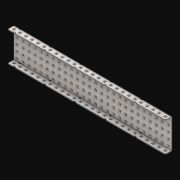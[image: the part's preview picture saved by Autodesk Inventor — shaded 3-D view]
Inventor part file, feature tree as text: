
AUTODESK INVENTOR PART (.ipt)
format: ipt  version: 2021 (Build 250183000, 183)  size: 3,637,248 bytes
history: native  units: in
note: dims shown in document units (in); Inventor stores cm internally (conversion verified against a paired STEP export)
features: extrude x183, other x182, sketch x4, thicken_offset x3, pattern_linear x3, imported_body x1
ambient origin geometry x8: Origin, YZ Plane, XZ Plane, XY Plane, X Axis, Y Axis, Z Axis, Center Point
bodies: Solid1 (feature_tree)
feature tree (376):
  thicken_offset  "Thicken1"
  thicken_offset  "Thicken2"
  thicken_offset  "Thicken3"
  pattern_linear  "Rectangular Pattern1"  Spacing1=0.001in  [1 undecoded]
  pattern_linear  "Rectangular Pattern2"  Spacing1=0.001in  [1 undecoded]
  pattern_linear  "Rectangular Pattern3"  Spacing1=0.182in  [1 undecoded]
  extrude  "Extrusion1"  Depth=0.063in TaperAngle=0.0deg
  sketch  "Sketch1"  dims[d0=0.001in]
  other  "Srf1"
  sketch  "Sketch2"  dims[d1=0.001in]
  other  "Srf2"
  sketch  "Sketch3"  dims[d2=0.001in]
  other  "Srf3"
  other  "Srf4"
  other  "Srf5"
  other  "Srf6"
  other  "Srf7"
  other  "Srf8"
  other  "Srf9"
  other  "Srf10"
  other  "Srf11"
  other  "Srf12"
  other  "Srf13"
  other  "Srf14"
  other  "Srf15"
  other  "Srf16"
  other  "Srf17"
  other  "Srf18"
  other  "Srf19"
  other  "Srf20"
  other  "Srf21"
  other  "Srf22"
  other  "Srf23"
  other  "Srf24"
  other  "Srf25"
  other  "Srf26"
  other  "Srf27"
  other  "Srf28"
  other  "Srf38"
  other  "Srf39"
  other  "Srf40"
  other  "Srf41"
  other  "Srf42"
  other  "Srf43"
  other  "Srf44"
  other  "Srf45"
  other  "Srf46"
  other  "Srf47"
  other  "Srf48"
  other  "Srf49"
  other  "Srf50"
  other  "Srf51"
  other  "Srf52"
  other  "Srf53"
  other  "Srf54"
  other  "Srf55"
  other  "Srf56"
  other  "Srf57"
  other  "Srf58"
  other  "Srf59"
  other  "Srf60"
  other  "Srf61"
  other  "Srf62"
  other  "Srf72"
  other  "Srf73"
  other  "Srf74"
  other  "Srf75"
  other  "Srf76"
  other  "Srf77"
  other  "Srf78"
  other  "Srf79"
  other  "Srf80"
  other  "Srf81"
  other  "Srf82"
  other  "Srf83"
  other  "Srf84"
  other  "Srf85"
  other  "Srf86"
  other  "Srf87"
  other  "Srf88"
  other  "Srf89"
  other  "Srf90"
  other  "Srf91"
  other  "Srf92"
  other  "Srf93"
  other  "Srf94"
  other  "Srf95"
  other  "Srf96"
  other  "Srf106"
  other  "Srf107"
  other  "Srf108"
  other  "Srf109"
  other  "Srf110"
  other  "Srf111"
  other  "Srf112"
  other  "Srf113"
  other  "Srf114"
  other  "Srf115"
  other  "Srf116"
  other  "Srf117"
  other  "Srf118"
  other  "Srf119"
  other  "Srf120"
  other  "Srf121"
  other  "Srf122"
  other  "Srf123"
  other  "Srf124"
  other  "Srf125"
  other  "Srf126"
  other  "Srf127"
  other  "Srf128"
  other  "Srf129"
  other  "Srf130"
  other  "Srf131"
  other  "Srf141"
  other  "Srf142"
  other  "Srf143"
  other  "Srf144"
  other  "Srf145"
  other  "Srf146"
  other  "Srf147"
  other  "Srf148"
  other  "Srf149"
  other  "Srf150"
  other  "Srf151"
  other  "Srf152"
  other  "Srf153"
  other  "Srf154"
  other  "Srf155"
  other  "Srf156"
  other  "Srf157"
  other  "Srf158"
  other  "Srf159"
  other  "Srf160"
  other  "Srf161"
  other  "Srf162"
  other  "Srf163"
  other  "Srf164"
  other  "Srf165"
  other  "Srf166"
  other  "Srf176"
  other  "Srf177"
  other  "Srf178"
  other  "Srf179"
  other  "Srf180"
  other  "Srf181"
  other  "Srf182"
  other  "Srf183"
  other  "Srf184"
  other  "Srf185"
  other  "Srf186"
  other  "Srf187"
  other  "Srf188"
  other  "Srf189"
  other  "Srf190"
  other  "Srf191"
  other  "Srf192"
  other  "Srf193"
  other  "Srf194"
  other  "Srf195"
  other  "Srf196"
  other  "Srf197"
  other  "Srf198"
  other  "Srf199"
  other  "Srf200"
  other  "Srf201"
  other  "Srf211"
  other  "Srf212"
  other  "Srf213"
  other  "Srf214"
  other  "Srf215"
  other  "Srf216"
  other  "Srf217"
  other  "Srf218"
  other  "Srf219"
  other  "Srf220"
  other  "Srf221"
  other  "Srf222"
  other  "Srf223"
  other  "Srf224"
  other  "Srf225"
  other  "Srf226"
  other  "Srf227"
  other  "Srf228"
  other  "Srf229"
  other  "Srf230"
  other  "Srf231"
  other  "Srf232"
  other  "Srf233"
  other  "Srf234"
  other  "Srf235"
  other  "Srf236"
  sketch  "Sketch4"  dims[d3=0.001in d4=0.001in d5=0.001in d6=0.182in d7=0.063in d8=0.0in d9=0.182in d10=0.063in d11=0.0in d12=0.182in d13=0.063in d14=0.0in d17=0.5in d18=10.2362in d20=0.5in d21=10.2362in d23=0.5in d24=1.9685in d26=0.5in d27=4.5in d28=0.0in]
  imported_body  "Imported1"
  extrude  "ExtrusionSrf1"  Depth=4.5in
  extrude  "ExtrusionSrf2"  Depth=0.063in TaperAngle=0.0deg
  extrude  "ExtrusionSrf3"  Depth=4.5in
  extrude  "ExtrusionSrf4"  Depth=0.063in TaperAngle=0.0deg
  extrude  "ExtrusionSrf5"  Depth=0.5in
  extrude  "ExtrusionSrf6"  Depth=4.5in
  extrude  "ExtrusionSrf7"  Depth=0.5in
  extrude  "ExtrusionSrf8"  Depth=4.5in
  extrude  "ExtrusionSrf9"  Depth=0.5in
  extrude  "ExtrusionSrf10"  Depth=0.5in
  extrude  "ExtrusionSrf11"  Depth=4.5in
  extrude  "ExtrusionSrf12"  TaperAngle=0.0deg  [1 undecoded]
  extrude  "ExtrusionSrf13"  [1 undecoded]
  extrude  "ExtrusionSrf14"  [1 undecoded]
  extrude  "ExtrusionSrf15"  [1 undecoded]
  extrude  "ExtrusionSrf16"  [1 undecoded]
  extrude  "ExtrusionSrf17"  [1 undecoded]
  extrude  "ExtrusionSrf18"  [1 undecoded]
  extrude  "ExtrusionSrf19"  [1 undecoded]
  extrude  "ExtrusionSrf20"  [1 undecoded]
  extrude  "ExtrusionSrf21"  [1 undecoded]
  extrude  "ExtrusionSrf22"  [1 undecoded]
  extrude  "ExtrusionSrf23"  [1 undecoded]
  extrude  "ExtrusionSrf24"  [1 undecoded]
  extrude  "ExtrusionSrf25"  [1 undecoded]
  extrude  "ExtrusionSrf26"  [1 undecoded]
  extrude  "ExtrusionSrf27"  [1 undecoded]
  extrude  "ExtrusionSrf28"  [1 undecoded]
  extrude  "ExtrusionSrf38"  [1 undecoded]
  extrude  "ExtrusionSrf39"  [1 undecoded]
  extrude  "ExtrusionSrf40"  [1 undecoded]
  extrude  "ExtrusionSrf41"  [1 undecoded]
  extrude  "ExtrusionSrf42"  [1 undecoded]
  extrude  "ExtrusionSrf43"  [1 undecoded]
  extrude  "ExtrusionSrf44"  [1 undecoded]
  extrude  "ExtrusionSrf45"  [1 undecoded]
  extrude  "ExtrusionSrf46"  [1 undecoded]
  extrude  "ExtrusionSrf47"  [1 undecoded]
  extrude  "ExtrusionSrf48"  [1 undecoded]
  extrude  "ExtrusionSrf49"  [1 undecoded]
  extrude  "ExtrusionSrf50"  [1 undecoded]
  extrude  "ExtrusionSrf51"  [1 undecoded]
  extrude  "ExtrusionSrf52"  [1 undecoded]
  extrude  "ExtrusionSrf53"  [1 undecoded]
  extrude  "ExtrusionSrf54"  [1 undecoded]
  extrude  "ExtrusionSrf55"  [1 undecoded]
  extrude  "ExtrusionSrf56"  [1 undecoded]
  extrude  "ExtrusionSrf57"  [1 undecoded]
  extrude  "ExtrusionSrf58"  [1 undecoded]
  extrude  "ExtrusionSrf59"  [1 undecoded]
  extrude  "ExtrusionSrf60"  [1 undecoded]
  extrude  "ExtrusionSrf61"  [1 undecoded]
  extrude  "ExtrusionSrf62"  [1 undecoded]
  extrude  "ExtrusionSrf72"  [1 undecoded]
  extrude  "ExtrusionSrf73"  [1 undecoded]
  extrude  "ExtrusionSrf74"  [1 undecoded]
  extrude  "ExtrusionSrf75"  [1 undecoded]
  extrude  "ExtrusionSrf76"  [1 undecoded]
  extrude  "ExtrusionSrf77"  [1 undecoded]
  extrude  "ExtrusionSrf78"  [1 undecoded]
  extrude  "ExtrusionSrf79"  [1 undecoded]
  extrude  "ExtrusionSrf80"  [1 undecoded]
  extrude  "ExtrusionSrf81"  [1 undecoded]
  extrude  "ExtrusionSrf82"  [1 undecoded]
  extrude  "ExtrusionSrf83"  [1 undecoded]
  extrude  "ExtrusionSrf84"  [1 undecoded]
  extrude  "ExtrusionSrf85"  [1 undecoded]
  extrude  "ExtrusionSrf86"  [1 undecoded]
  extrude  "ExtrusionSrf87"  [1 undecoded]
  extrude  "ExtrusionSrf88"  [1 undecoded]
  extrude  "ExtrusionSrf89"  [1 undecoded]
  extrude  "ExtrusionSrf90"  [1 undecoded]
  extrude  "ExtrusionSrf91"  [1 undecoded]
  extrude  "ExtrusionSrf92"  [1 undecoded]
  extrude  "ExtrusionSrf93"  [1 undecoded]
  extrude  "ExtrusionSrf94"  [1 undecoded]
  extrude  "ExtrusionSrf95"  [1 undecoded]
  extrude  "ExtrusionSrf96"  [1 undecoded]
  extrude  "ExtrusionSrf106"  [1 undecoded]
  extrude  "ExtrusionSrf107"  [1 undecoded]
  extrude  "ExtrusionSrf108"  [1 undecoded]
  extrude  "ExtrusionSrf109"  [1 undecoded]
  extrude  "ExtrusionSrf110"  [1 undecoded]
  extrude  "ExtrusionSrf111"  [1 undecoded]
  extrude  "ExtrusionSrf112"  [1 undecoded]
  extrude  "ExtrusionSrf113"  [1 undecoded]
  extrude  "ExtrusionSrf114"  [1 undecoded]
  extrude  "ExtrusionSrf115"  [1 undecoded]
  extrude  "ExtrusionSrf116"  [1 undecoded]
  extrude  "ExtrusionSrf117"  [1 undecoded]
  extrude  "ExtrusionSrf118"  [1 undecoded]
  extrude  "ExtrusionSrf119"  [1 undecoded]
  extrude  "ExtrusionSrf120"  [1 undecoded]
  extrude  "ExtrusionSrf121"  [1 undecoded]
  extrude  "ExtrusionSrf122"  [1 undecoded]
  extrude  "ExtrusionSrf123"  [1 undecoded]
  extrude  "ExtrusionSrf124"  [1 undecoded]
  extrude  "ExtrusionSrf125"  [1 undecoded]
  extrude  "ExtrusionSrf126"  [1 undecoded]
  extrude  "ExtrusionSrf127"  [1 undecoded]
  extrude  "ExtrusionSrf128"  [1 undecoded]
  extrude  "ExtrusionSrf129"  [1 undecoded]
  extrude  "ExtrusionSrf130"  [1 undecoded]
  extrude  "ExtrusionSrf131"  [1 undecoded]
  extrude  "ExtrusionSrf141"  [1 undecoded]
  extrude  "ExtrusionSrf142"  [1 undecoded]
  extrude  "ExtrusionSrf143"  [1 undecoded]
  extrude  "ExtrusionSrf144"  [1 undecoded]
  extrude  "ExtrusionSrf145"  [1 undecoded]
  extrude  "ExtrusionSrf146"  [1 undecoded]
  extrude  "ExtrusionSrf147"  [1 undecoded]
  extrude  "ExtrusionSrf148"  [1 undecoded]
  extrude  "ExtrusionSrf149"  [1 undecoded]
  extrude  "ExtrusionSrf150"  [1 undecoded]
  extrude  "ExtrusionSrf151"  [1 undecoded]
  extrude  "ExtrusionSrf152"  [1 undecoded]
  extrude  "ExtrusionSrf153"  [1 undecoded]
  extrude  "ExtrusionSrf154"  [1 undecoded]
  extrude  "ExtrusionSrf155"  [1 undecoded]
  extrude  "ExtrusionSrf156"  [1 undecoded]
  extrude  "ExtrusionSrf157"  [1 undecoded]
  extrude  "ExtrusionSrf158"  [1 undecoded]
  extrude  "ExtrusionSrf159"  [1 undecoded]
  extrude  "ExtrusionSrf160"  [1 undecoded]
  extrude  "ExtrusionSrf161"  [1 undecoded]
  extrude  "ExtrusionSrf162"  [1 undecoded]
  extrude  "ExtrusionSrf163"  [1 undecoded]
  extrude  "ExtrusionSrf164"  [1 undecoded]
  extrude  "ExtrusionSrf165"  [1 undecoded]
  extrude  "ExtrusionSrf166"  [1 undecoded]
  extrude  "ExtrusionSrf176"  [1 undecoded]
  extrude  "ExtrusionSrf177"  [1 undecoded]
  extrude  "ExtrusionSrf178"  [1 undecoded]
  extrude  "ExtrusionSrf179"  [1 undecoded]
  extrude  "ExtrusionSrf180"  [1 undecoded]
  extrude  "ExtrusionSrf181"  [1 undecoded]
  extrude  "ExtrusionSrf182"  [1 undecoded]
  extrude  "ExtrusionSrf183"  [1 undecoded]
  extrude  "ExtrusionSrf184"  [1 undecoded]
  extrude  "ExtrusionSrf185"  [1 undecoded]
  extrude  "ExtrusionSrf186"  [1 undecoded]
  extrude  "ExtrusionSrf187"  [1 undecoded]
  extrude  "ExtrusionSrf188"  [1 undecoded]
  extrude  "ExtrusionSrf189"  [1 undecoded]
  extrude  "ExtrusionSrf190"  [1 undecoded]
  extrude  "ExtrusionSrf191"  [1 undecoded]
  extrude  "ExtrusionSrf192"  [1 undecoded]
  extrude  "ExtrusionSrf193"  [1 undecoded]
  extrude  "ExtrusionSrf194"  [1 undecoded]
  extrude  "ExtrusionSrf195"  [1 undecoded]
  extrude  "ExtrusionSrf196"  [1 undecoded]
  extrude  "ExtrusionSrf197"  [1 undecoded]
  extrude  "ExtrusionSrf198"  [1 undecoded]
  extrude  "ExtrusionSrf199"  [1 undecoded]
  extrude  "ExtrusionSrf200"  [1 undecoded]
  extrude  "ExtrusionSrf201"  [1 undecoded]
  extrude  "ExtrusionSrf211"  [1 undecoded]
  extrude  "ExtrusionSrf212"  [1 undecoded]
  extrude  "ExtrusionSrf213"  [1 undecoded]
  extrude  "ExtrusionSrf214"  [1 undecoded]
  extrude  "ExtrusionSrf215"  [1 undecoded]
  extrude  "ExtrusionSrf216"  [1 undecoded]
  extrude  "ExtrusionSrf217"  [1 undecoded]
  extrude  "ExtrusionSrf218"  [1 undecoded]
  extrude  "ExtrusionSrf219"  [1 undecoded]
  extrude  "ExtrusionSrf220"  [1 undecoded]
  extrude  "ExtrusionSrf221"  [1 undecoded]
  extrude  "ExtrusionSrf222"  [1 undecoded]
  extrude  "ExtrusionSrf223"  [1 undecoded]
  extrude  "ExtrusionSrf224"  [1 undecoded]
  extrude  "ExtrusionSrf225"  [1 undecoded]
  extrude  "ExtrusionSrf226"  [1 undecoded]
  extrude  "ExtrusionSrf227"  [1 undecoded]
  extrude  "ExtrusionSrf228"  [1 undecoded]
  extrude  "ExtrusionSrf229"  [1 undecoded]
  extrude  "ExtrusionSrf230"  [1 undecoded]
  extrude  "ExtrusionSrf231"  [1 undecoded]
  extrude  "ExtrusionSrf232"  [1 undecoded]
  extrude  "ExtrusionSrf233"  [1 undecoded]
  extrude  "ExtrusionSrf234"  [1 undecoded]
  extrude  "ExtrusionSrf235"  [1 undecoded]
  extrude  "ExtrusionSrf236"  [1 undecoded]
note: 174 required parameter values undecoded (feature->parameter linkage not recoverable at this tier; creation-order binding heuristic only, values carry confidence <= 0.55)
